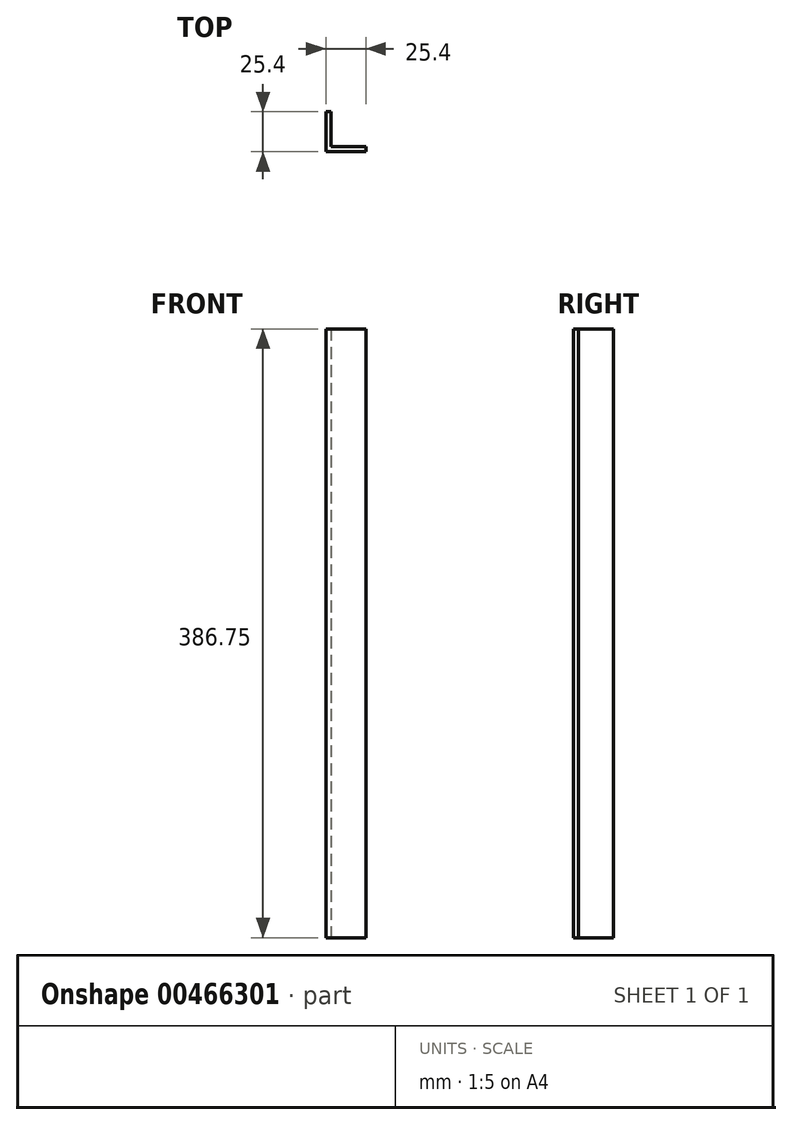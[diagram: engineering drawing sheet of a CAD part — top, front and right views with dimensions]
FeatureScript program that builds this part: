
annotation { "Feature Type Name" : "Feature", "Feature Type Description" : "" }
export const myFeature = defineFeature(function(context is Context, id is Id, definition is map)
    precondition{}
    {
        {
            var Q0;
            Q0=qCreatedBy(makeId("Top.planeOp"),FACE);
            var sketch = newSketch(context, id + "F0", { "sketchPlane" : qUnion([Q0])});
            skLineSegment(sketch, "E0", {"start": v(-32.36, 10.96) * mm, "end": v(-6.96, 10.96) * mm});
            skLineSegment(sketch, "E1", {"start": v(-32.36, 10.96) * mm, "end": v(-32.36, 36.36) * mm});
            skLineSegment(sketch, "E2", {"start": v(-32.36, 36.36) * mm, "end": v(-29.19, 36.36) * mm});
            skLineSegment(sketch, "E3", {"start": v(-29.19, 36.36) * mm, "end": v(-29.19, 14.13) * mm});
            skLineSegment(sketch, "E4", {"start": v(-29.19, 14.13) * mm, "end": v(-6.96, 14.13) * mm});
            skLineSegment(sketch, "E5", {"start": v(-6.96, 14.13) * mm, "end": v(-6.96, 10.96) * mm});
            skSolve(sketch);
        }
        {
            var Q0;
            Q0=makeQuery(id+"F0.imprint","IMPRINT",FACE,{"disambiguationData":[TD([[makeQuery(id+"F0.imprint","IMPRINT",EDGE,{"derivedFrom":sQuery(id+"F0.wireOp",EDGE,"E0")}),1.0]])]});
            extrude(context, id + "F1", {"entities" : qUnion([Q0]), "depth" : 386.75 * mm});
        }
    });
